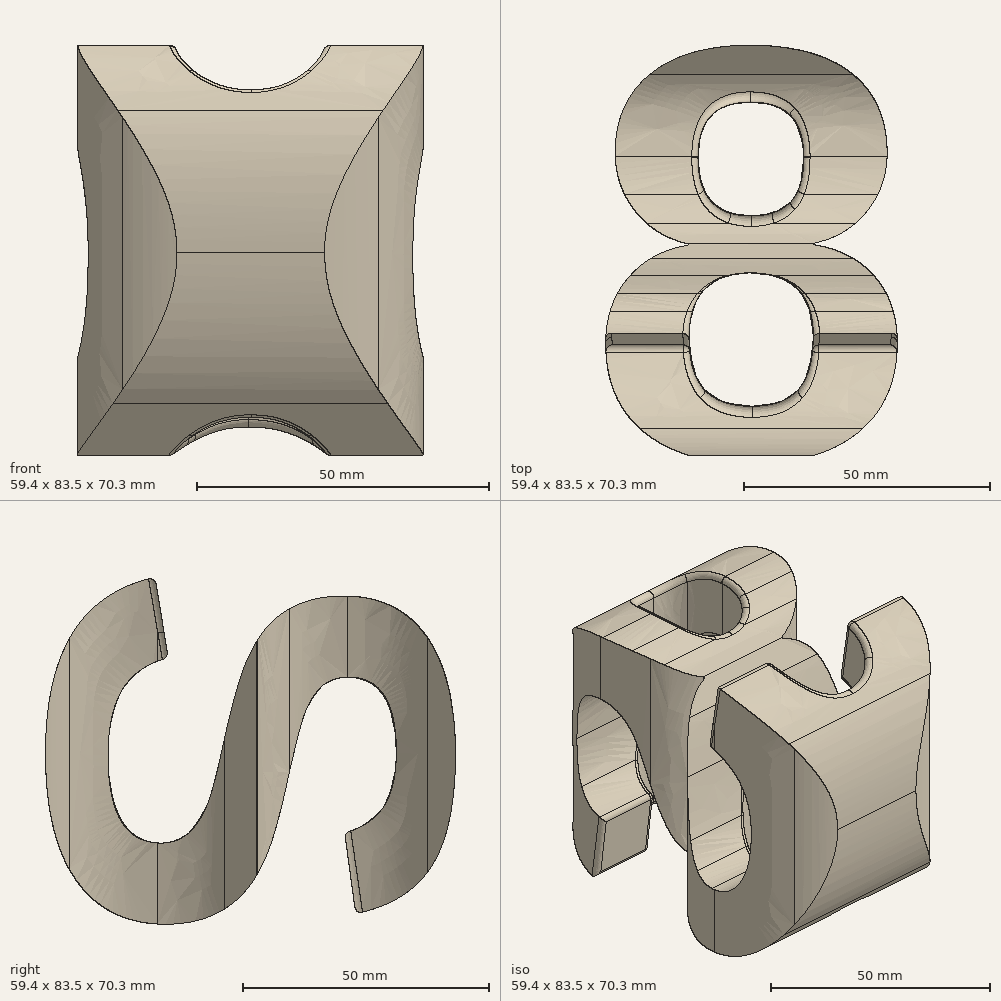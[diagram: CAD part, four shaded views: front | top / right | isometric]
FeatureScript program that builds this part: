
annotation { "Feature Type Name" : "Feature", "Feature Type Description" : "" }
export const myFeature = defineFeature(function(context is Context, id is Id, definition is map)
    precondition{}
    {
        {
            var Q0;
            Q0=qCreatedBy(makeId("Top.planeOp"),FACE);
            var sketch = newSketch(context, id + "F0", { "sketchPlane" : qUnion([Q0])});
            skLineSegment(sketch, "E0.bottom", {"start": v(44.45, 44.45) * mm, "end": v(-44.45, 44.45) * mm});
            skLineSegment(sketch, "E0.top", {"start": v(44.45, -44.45) * mm, "end": v(-44.45, -44.45) * mm});
            skLineSegment(sketch, "E0.left", {"start": v(44.45, 44.45) * mm, "end": v(44.45, -44.45) * mm});
            skLineSegment(sketch, "E0.right", {"start": v(-44.45, 44.45) * mm, "end": v(-44.45, -44.45) * mm});
            skPoint(sketch, "E0.middle", {"position": v(0, 0) * mm});
            skSolve(sketch);
        }
        {
            var Q0;
            Q0 = qSketchRegion(id + "F0", true);
            extrude(context, id + "F1", {"entities" : qUnion([Q0]), "endBound" : BoundingType.SYMMETRIC, "depth" : 88.9 * mm, "offsetDistance" : 25.4 * mm});
        }
        {
            var Q0;
            Q0=makeQuery(id+"F1.opExtrude","CAP_FACE",FACE,{"disambiguationData":[OSD([sQuery(id+"F0.wireOp",EDGE,"E0.bottom"),sQuery(id+"F0.wireOp",EDGE,"E0.top"),sQuery(id+"F0.wireOp",EDGE,"E0.left"),sQuery(id+"F0.wireOp",EDGE,"E0.right")])],"isStart":false});
            var sketch = newSketch(context, id + "F2", { "sketchPlane" : qUnion([Q0])});
            skText(sketch, "E1", { "text": "8", "fontName": "Arimo-Bold.ttf"});
            skLineSegment(sketch, "E2.bottom", {"start": v(58.83, 51.68) * mm, "end": v(-58.83, 51.68) * mm});
            skLineSegment(sketch, "E2.top", {"start": v(58.83, -51.68) * mm, "end": v(-58.83, -51.68) * mm});
            skLineSegment(sketch, "E2.left", {"start": v(58.83, 51.68) * mm, "end": v(58.83, -51.68) * mm});
            skLineSegment(sketch, "E2.right", {"start": v(-58.83, 51.68) * mm, "end": v(-58.83, -51.68) * mm});
            skPoint(sketch, "E2.middle", {"position": v(0, 0) * mm});
            const initialGuessF2  = {"E1": [-0.03331, -0.04213, 1, 0, 0.08658]};
            skSetInitialGuess(sketch, initialGuessF2);
            skSolve(sketch);
        }
        {
            var Q0;
            Q0=makeQuery(id+"F2.imprint","IMPRINT",FACE,{"disambiguationData":[TD([[makeQuery(id+"F2.imprint","IMPRINT",EDGE,{"derivedFrom":sQuery(id+"F2.wireOp",EDGE,"E2.bottom")}),1.0]])]});
            var Q1;
            Q1=makeQuery(id+"F2.imprint","IMPRINT",FACE,{"disambiguationData":[TD([[makeQuery(id+"F2.imprint","IMPRINT",EDGE,{"derivedFrom":sQuery(id+"F2.wireOp",EDGE,"E1.sketch_text.stroke-0")}),1.0]])]});
            var Q2;
            Q2=makeQuery(id+"F2.imprint","IMPRINT",FACE,{"disambiguationData":[TD([[makeQuery(id+"F2.imprint","IMPRINT",EDGE,{"derivedFrom":sQuery(id+"F2.wireOp",EDGE,"E1.sketch_text.stroke-24")}),1.0]])]});
            var Q3;
            Q3=makeQuery(id+"F2.imprint","IMPRINT",FACE,{"disambiguationData":[TD([[makeQuery(id+"F2.imprint","IMPRINT",EDGE,{"derivedFrom":sQuery(id+"F2.wireOp",EDGE,"E1.sketch_text.stroke-18")}),1.0]])]});
            extrude(context, id + "F3", {"entities" : qUnion([Q0, Q1, Q2, Q3]), "operationType" : NewBodyOperationType.REMOVE, "oppositeDirection" : true, "depth" : 101.6 * mm, "offsetDistance" : 25.4 * mm});
        }
        {
            var Q0;
            Q0=qCreatedBy(makeId("Right.planeOp"),FACE);
            var sketch = newSketch(context, id + "F4", { "sketchPlane" : qUnion([Q0])});
            skText(sketch, "E3", { "text": "S", "fontName": "Arimo-Bold.ttf"});
            skLineSegment(sketch, "E4.bottom", {"start": v(-63.87, -79.53) * mm, "end": v(201.95, -79.53) * mm});
            skLineSegment(sketch, "E4.top", {"start": v(-63.87, 227.22) * mm, "end": v(201.95, 227.22) * mm});
            skLineSegment(sketch, "E4.left", {"start": v(-63.87, -79.53) * mm, "end": v(-63.87, 227.22) * mm});
            skLineSegment(sketch, "E4.right", {"start": v(201.95, -79.53) * mm, "end": v(201.95, 227.22) * mm});
            skPoint(sketch, "E4.middle", {"position": v(69.04, 73.85) * mm});
            const initialGuessF4  = {"E3": [-0.04053, 0.0411, 0, -1, 0.08488]};
            skSetInitialGuess(sketch, initialGuessF4);
            skSolve(sketch);
        }
        {
            var Q0;
            Q0=makeQuery(id+"F4.imprint","IMPRINT",FACE,{"disambiguationData":[TD([[makeQuery(id+"F4.imprint","IMPRINT",EDGE,{"derivedFrom":sQuery(id+"F4.wireOp",EDGE,"E3.sketch_text.stroke-0")}),1.0]])]});
            extrude(context, id + "F5", {"entities" : qUnion([Q0]), "operationType" : NewBodyOperationType.REMOVE, "endBound" : BoundingType.SYMMETRIC, "oppositeDirection" : true, "depth" : 101.6 * mm, "offsetDistance" : 25.4 * mm});
        }
        {
            var Q0;
            Q0=makeQuery(id+"F3.boolean.opBoolean","COPY",EDGE,{"derivedFrom":makeQuery(id+"F3.opExtrude","SWEPT_EDGE",EDGE,{"disambiguationData":[OSD([sQuery(id+"F2.wireOp",EDGE,"E1.sketch_text.stroke-15"),sQuery(id+"F2.wireOp",EDGE,"E1.sketch_text.stroke-16")])]})});
            var Q1;
            Q1=makeQuery(id+"F3.boolean.opBoolean","COPY",EDGE,{"derivedFrom":makeQuery(id+"F3.opExtrude","SWEPT_EDGE",EDGE,{"disambiguationData":[OSD([sQuery(id+"F2.wireOp",EDGE,"E1.sketch_text.stroke-14"),sQuery(id+"F2.wireOp",EDGE,"E1.sketch_text.stroke-15")])]})});
            var Q2;
            Q2=makeQuery(id+"F3.boolean.opBoolean","COPY",EDGE,{"derivedFrom":makeQuery(id+"F3.opExtrude","SWEPT_EDGE",EDGE,{"disambiguationData":[OSD([sQuery(id+"F2.wireOp",EDGE,"E1.sketch_text.stroke-6"),sQuery(id+"F2.wireOp",EDGE,"E1.sketch_text.stroke-7")])]})});
            var Q3;
            Q3=makeQuery(id+"F3.boolean.opBoolean","COPY",EDGE,{"derivedFrom":makeQuery(id+"F3.opExtrude","SWEPT_EDGE",EDGE,{"disambiguationData":[OSD([sQuery(id+"F2.wireOp",EDGE,"E1.sketch_text.stroke-5"),sQuery(id+"F2.wireOp",EDGE,"E1.sketch_text.stroke-6")])]})});
            fillet(context, id + "F6", {"entities" : qUnion([Q0, Q1, Q2, Q3]), "radius" : 0.25 * mm, "tangentPropagation" : true, "allowEdgeOverflow" : false});
        }
        {
            var Q0;
            Q0=makeQuery(id+"F5.boolean.opBoolean","COPY",FACE,{"disambiguationData":[TD([makeQuery(id+"F3.boolean.opBoolean","COPY",FACE,{"derivedFrom":makeQuery(id+"F3.opExtrude","SWEPT_FACE",FACE,{"disambiguationData":[OSD([sQuery(id+"F2.wireOp",EDGE,"E1.sketch_text.stroke-12")])]})})])],"derivedFrom":makeQuery(id+"F5.opExtrude","SWEPT_FACE",FACE,{"disambiguationData":[OSD([sQuery(id+"F4.wireOp",EDGE,"E3.sketch_text.stroke-20")])]})});
            var Q1;
            Q1=makeQuery(id+"F5.boolean.opBoolean","COPY",FACE,{"disambiguationData":[TD([makeQuery(id+"F3.boolean.opBoolean","COPY",FACE,{"derivedFrom":makeQuery(id+"F3.opExtrude","SWEPT_FACE",FACE,{"disambiguationData":[OSD([sQuery(id+"F2.wireOp",EDGE,"E1.sketch_text.stroke-8")])]})})])],"derivedFrom":makeQuery(id+"F5.opExtrude","SWEPT_FACE",FACE,{"disambiguationData":[OSD([sQuery(id+"F4.wireOp",EDGE,"E3.sketch_text.stroke-20")])]})});
            var Q2;
            Q2=makeQuery(id+"F5.boolean.opBoolean","COPY",FACE,{"disambiguationData":[TD([makeQuery(id+"F3.boolean.opBoolean","COPY",FACE,{"derivedFrom":makeQuery(id+"F3.opExtrude","SWEPT_FACE",FACE,{"disambiguationData":[OSD([sQuery(id+"F2.wireOp",EDGE,"E1.sketch_text.stroke-3")])]})})])],"derivedFrom":makeQuery(id+"F5.opExtrude","SWEPT_FACE",FACE,{"disambiguationData":[OSD([sQuery(id+"F4.wireOp",EDGE,"E3.sketch_text.stroke-4")])]})});
            var Q3;
            Q3=makeQuery(id+"F5.boolean.opBoolean","COPY",FACE,{"disambiguationData":[TD([makeQuery(id+"F3.boolean.opBoolean","COPY",FACE,{"derivedFrom":makeQuery(id+"F3.opExtrude","SWEPT_FACE",FACE,{"disambiguationData":[OSD([sQuery(id+"F2.wireOp",EDGE,"E1.sketch_text.stroke-0")])]})})])],"derivedFrom":makeQuery(id+"F5.opExtrude","SWEPT_FACE",FACE,{"disambiguationData":[OSD([sQuery(id+"F4.wireOp",EDGE,"E3.sketch_text.stroke-4")])]})});
            var Q4;
            Q4=makeQuery(id+"F5.boolean.opBoolean","INTERSECT",EDGE,{"derivedFrom":[makeQuery(id+"F3.boolean.opBoolean","COPY",FACE,{"derivedFrom":makeQuery(id+"F3.opExtrude","SWEPT_FACE",FACE,{"disambiguationData":[OSD([sQuery(id+"F2.wireOp",EDGE,"E1.sketch_text.stroke-20")])]})}),makeQuery(id+"F5.opExtrude","SWEPT_FACE",FACE,{"disambiguationData":[OSD([sQuery(id+"F4.wireOp",EDGE,"E3.sketch_text.stroke-16")])]})]});
            var Q5;
            Q5=makeQuery(id+"F5.boolean.opBoolean","INTERSECT",EDGE,{"derivedFrom":[makeQuery(id+"F3.boolean.opBoolean","COPY",FACE,{"derivedFrom":makeQuery(id+"F3.opExtrude","SWEPT_FACE",FACE,{"disambiguationData":[OSD([sQuery(id+"F2.wireOp",EDGE,"E1.sketch_text.stroke-24")])]})}),makeQuery(id+"F5.opExtrude","SWEPT_FACE",FACE,{"disambiguationData":[OSD([sQuery(id+"F4.wireOp",EDGE,"E3.sketch_text.stroke-29")])]})]});
            var Q6;
            Q6=makeQuery(id+"F5.boolean.opBoolean","INTERSECT",EDGE,{"derivedFrom":[makeQuery(id+"F3.boolean.opBoolean","COPY",FACE,{"derivedFrom":makeQuery(id+"F3.opExtrude","SWEPT_FACE",FACE,{"disambiguationData":[OSD([sQuery(id+"F2.wireOp",EDGE,"E1.sketch_text.stroke-20")])]})}),makeQuery(id+"F5.opExtrude","SWEPT_FACE",FACE,{"disambiguationData":[OSD([sQuery(id+"F4.wireOp",EDGE,"E3.sketch_text.stroke-19")])]})]});
            var Q7;
            Q7=makeQuery(id+"F5.boolean.opBoolean","INTERSECT",EDGE,{"derivedFrom":[makeQuery(id+"F3.boolean.opBoolean","COPY",FACE,{"derivedFrom":makeQuery(id+"F3.opExtrude","SWEPT_FACE",FACE,{"disambiguationData":[OSD([sQuery(id+"F2.wireOp",EDGE,"E1.sketch_text.stroke-30")])]})}),makeQuery(id+"F5.opExtrude","SWEPT_FACE",FACE,{"disambiguationData":[OSD([sQuery(id+"F4.wireOp",EDGE,"E3.sketch_text.stroke-3")])]})]});
            var Q8;
            Q8=makeQuery(id+"F5.boolean.opBoolean","INTERSECT",EDGE,{"derivedFrom":[makeQuery(id+"F3.boolean.opBoolean","COPY",FACE,{"derivedFrom":makeQuery(id+"F3.opExtrude","SWEPT_FACE",FACE,{"disambiguationData":[OSD([sQuery(id+"F2.wireOp",EDGE,"E1.sketch_text.stroke-29")])]})}),makeQuery(id+"F5.opExtrude","SWEPT_FACE",FACE,{"disambiguationData":[OSD([sQuery(id+"F4.wireOp",EDGE,"E3.sketch_text.stroke-6")])]})]});
            var Q9;
            Q9=makeQuery(id+"F5.boolean.opBoolean","INTERSECT",EDGE,{"derivedFrom":[makeQuery(id+"F3.boolean.opBoolean","COPY",FACE,{"derivedFrom":makeQuery(id+"F3.opExtrude","SWEPT_FACE",FACE,{"disambiguationData":[OSD([sQuery(id+"F2.wireOp",EDGE,"E1.sketch_text.stroke-27")])]})}),makeQuery(id+"F5.opExtrude","SWEPT_FACE",FACE,{"disambiguationData":[OSD([sQuery(id+"F4.wireOp",EDGE,"E3.sketch_text.stroke-5")])]})]});
            var Q10;
            Q10=makeQuery(id+"F5.boolean.opBoolean","INTERSECT",EDGE,{"derivedFrom":[makeQuery(id+"F3.boolean.opBoolean","COPY",FACE,{"derivedFrom":makeQuery(id+"F3.opExtrude","SWEPT_FACE",FACE,{"disambiguationData":[OSD([sQuery(id+"F2.wireOp",EDGE,"E1.sketch_text.stroke-22")])]})}),makeQuery(id+"F5.opExtrude","SWEPT_FACE",FACE,{"disambiguationData":[OSD([sQuery(id+"F4.wireOp",EDGE,"E3.sketch_text.stroke-27")])]})]});
            fillet(context, id + "F7", {"entities" : qUnion([Q0, Q1, Q2, Q3, Q4, Q5, Q6, Q7, Q8, Q9, Q10]), "radius" : 1.27 * mm, "tangentPropagation" : true, "allowEdgeOverflow" : false});
        }
        {
            var Q0;
            Q0=makeQuery(id+"F5.boolean.opBoolean","INTERSECT",EDGE,{"derivedFrom":[makeQuery(id+"F3.boolean.opBoolean","COPY",FACE,{"derivedFrom":makeQuery(id+"F3.opExtrude","SWEPT_FACE",FACE,{"disambiguationData":[OSD([sQuery(id+"F2.wireOp",EDGE,"E1.sketch_text.stroke-20")])]})}),makeQuery(id+"F5.opExtrude","SWEPT_FACE",FACE,{"disambiguationData":[OSD([sQuery(id+"F4.wireOp",EDGE,"E3.sketch_text.stroke-23")])]})]});
            var Q1;
            Q1=makeQuery(id+"F5.boolean.opBoolean","INTERSECT",EDGE,{"derivedFrom":[makeQuery(id+"F3.boolean.opBoolean","COPY",FACE,{"derivedFrom":makeQuery(id+"F3.opExtrude","SWEPT_FACE",FACE,{"disambiguationData":[OSD([sQuery(id+"F2.wireOp",EDGE,"E1.sketch_text.stroke-18")])]})}),makeQuery(id+"F5.opExtrude","SWEPT_FACE",FACE,{"disambiguationData":[OSD([sQuery(id+"F4.wireOp",EDGE,"E3.sketch_text.stroke-23")])]})]});
            fillet(context, id + "F8", {"entities" : qUnion([Q0, Q1]), "radius" : 1.27 * mm, "tangentPropagation" : true, "allowEdgeOverflow" : false});
        }
    });
